# Revit family: Storage-Teknion-CTAE_Single_Side_Access_Tower_Elevated-R2021
name_source: partatom
category: Furniture
units: mm (PartAtom-declared; Revit-internal decimal feet)

## family parameters
Always vertical = Yes
Cut with Voids When Loaded = No
OmniClass Number = 23.40.20.00
OmniClass Title = General Furniture and Specialties
Room Calculation Point = No
Shared = Yes
Work Plane-Based = No

## types (4) — shared parameters
Assembly Code = E2020200
Height Option = Select Height Option. 5E - 5 High Elevated (70.25 Inch) are default.
Manufacturer = Teknion
Manufacturer Fax = 416.661.4586
Part Number = CTAE
Product Documentation Link = https://www.teknion.com
Product Line = Bookcases, Stackers & Towers
Product Page URL = https://www.teknion.com
Series = Chronicle
Shelf 1 = Yes
Shelf 5/Top 5E = Yes
Sustainability Data = https://www.teknion.com
URL = www.teknion.com
Unit Weight URL = http://www.teknion.com
Warranty = http://www.teknion.com
Width = 18 "
zero-valued in all types: Default Elevation

## per-type parameters (varying)
| type | 5E - 5 High Elevated (70.25" Height) | 6E - 6 High Elevated (84" Height) | Description | Model | SF - Side Access Shelves Full Height | SW - Side Access Open Wardrobe Full | Shelf 2 | Shelf 3 | Shelf 4 | Shelf 5/Top 6E - Front Distance | Top - 6E |
| Side Access Shelves Full Height (SF), 5 High Elevated (70.25" Height) | Yes | No | Single Side Access Tower, Elevated, Side Access Shelves Full Height Configuration, 5 High Elevated (70.25" Height), 18" Width | CTAESF5E_18_ | Yes | No | Yes | Yes | Yes | 0 " | No |
| Side Access Shelves Full Height (SF), 6 High Elevated (84" Height) | No | Yes | Single Side Access Tower, Elevated, Side Access Shelves Full Height Configuration, 6 High Elevated (84" Height), 18" Width | CTAESF6E_18_ | Yes | No | Yes | Yes | Yes | 1 " | Yes |
| Side Access Open Wardrobe Full (SW), 6 High Elevated (84" Height) | No | Yes | Single Side Access Tower, Elevated, Side Access Open Wardrobe Full Configuration, 6 High Elevated (84" Height), 18" Width | CTAESW6E_18_ | No | Yes | No | No | No | 1 " | Yes |
| Side Access Open Wardrobe Full (SW), 5 High Elevated (70.25" Height) | Yes | No | Single Side Access Tower, Elevated, Side Access Open Wardrobe Full Configuration, 5 High Elevated (70.25" Height), 18" Width | CTAESW5E_18_ | No | Yes | No | No | Yes | 0 " | No |

## geometry (parser evidence)
native form markers: Sweep x4
no freeform markers — native parametric forms only
